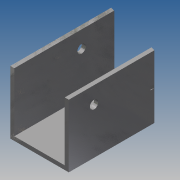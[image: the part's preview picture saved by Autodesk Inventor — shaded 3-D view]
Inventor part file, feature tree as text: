
AUTODESK INVENTOR PART (.ipt)
format: ipt  version: 2014 SP1 (Build 180222100, 222)  size: 116,224 bytes
history: native  units: in
note: dims shown in document units (in); Inventor stores cm internally (conversion verified against a paired STEP export)
features: sketch x5, other x3, plane x1
ambient origin geometry x8: Origin, YZ Plane, XZ Plane, XY Plane, X Axis, Y Axis, Z Axis, Center Point
bodies: Solid1 (feature_tree)
feature tree (9):
  other  "endChannel.ipt"
  other  "Solid1::endChannel.ipt"
  other  "TaggingFeature1"
  sketch  "Sketch1"  dims[d0=0.3937in]
  sketch  "Sketch2"  dims[d1=1.75in d2=1.75in d3=0.12in d4=3.0in d5=0.0in d6=2.0in d7=0.1006in d8=4.0in d9=0.0in d10=0.75in d11=0.5in d12=0.25in d17=1.0in d18=0.8108in d19=2.0in d20=0.5in d21=0.25in d26=1.0in d27=0.8108in d28=90.0deg d29=0.1in d30=0.1in d31=4.0in d32=0.0in]
  sketch  "Sketch3"
  sketch  "Sketch5"
  sketch  "Sketch6"
  plane  "Work Plane1"
